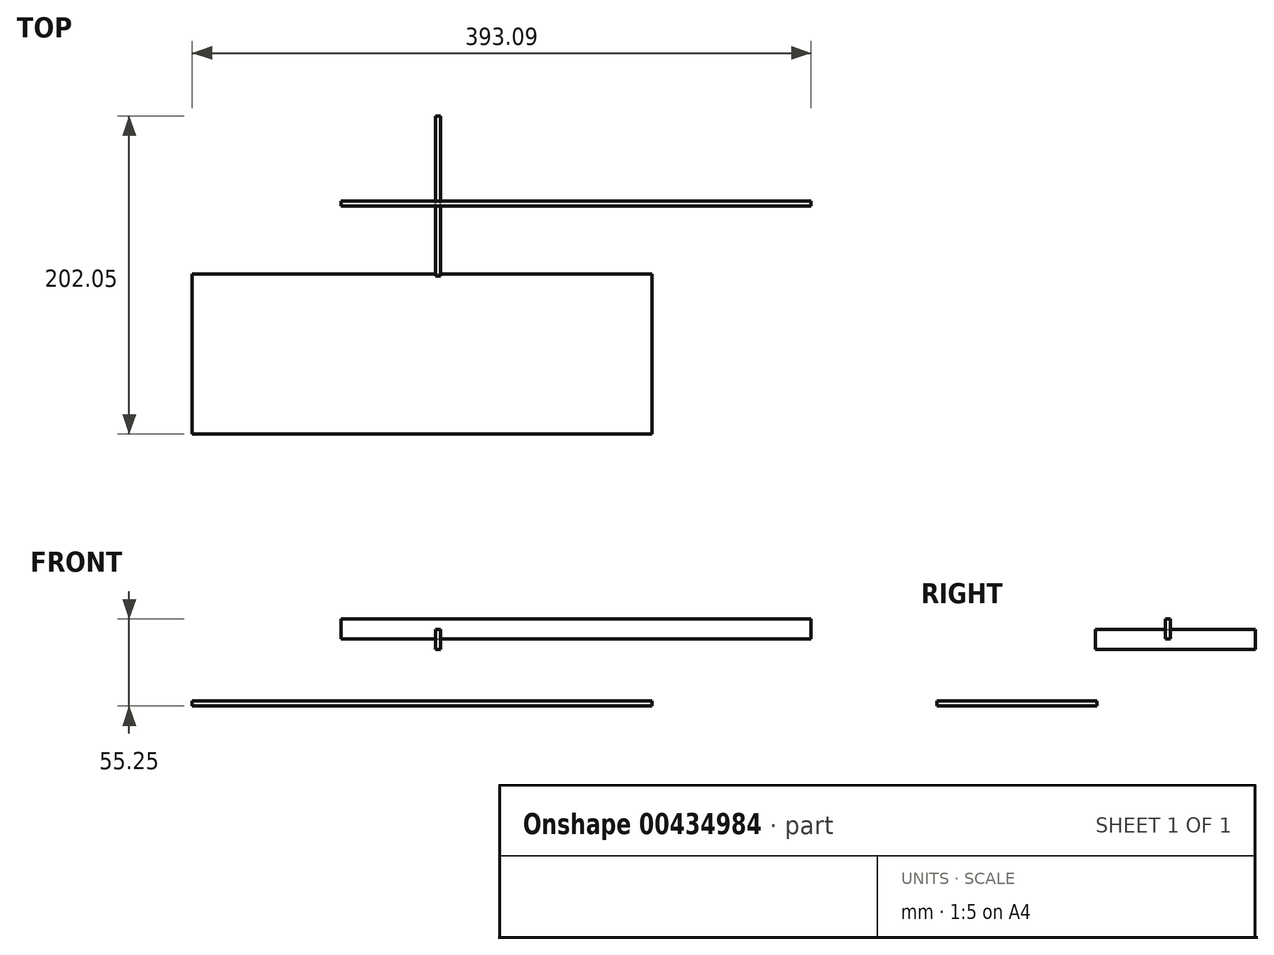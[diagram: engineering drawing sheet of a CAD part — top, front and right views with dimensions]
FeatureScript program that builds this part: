
annotation { "Feature Type Name" : "Feature", "Feature Type Description" : "" }
export const myFeature = defineFeature(function(context is Context, id is Id, definition is map)
    precondition{}
    {
        {
            var Q0;
            Q0=qCreatedBy(makeId("Top.planeOp"),FACE);
            var sketch = newSketch(context, id + "F0", { "sketchPlane" : qUnion([Q0])});
            skLineSegment(sketch, "E0.bottom", {"start": v(-154.5, -148.06) * mm, "end": v(137.6, -148.06) * mm});
            skLineSegment(sketch, "E0.top", {"start": v(-154.5, -46.46) * mm, "end": v(137.6, -46.46) * mm});
            skLineSegment(sketch, "E0.left", {"start": v(-154.5, -148.06) * mm, "end": v(-154.5, -46.46) * mm});
            skLineSegment(sketch, "E0.right", {"start": v(137.6, -148.06) * mm, "end": v(137.6, -46.46) * mm});
            skSolve(sketch);
        }
        {
            var Q0;
            Q0=makeQuery(id+"F0.imprint","IMPRINT",FACE,{"disambiguationData":[TD([[makeQuery(id+"F0.imprint","IMPRINT",EDGE,{"derivedFrom":sQuery(id+"F0.wireOp",EDGE,"E0.bottom")}),1.0]])]});
            extrude(context, id + "F1", {"entities" : qUnion([Q0]), "depth" : 3.17 * mm});
        }
        {
            var Q0;
            Q0=qCreatedBy(makeId("Front.planeOp"),FACE);
            var sketch = newSketch(context, id + "F2", { "sketchPlane" : qUnion([Q0])});
            skLineSegment(sketch, "E1.bottom", {"start": v(-59.85, 55.25) * mm, "end": v(238.6, 55.25) * mm});
            skLineSegment(sketch, "E1.top", {"start": v(-59.85, 42.55) * mm, "end": v(238.6, 42.55) * mm});
            skLineSegment(sketch, "E1.left", {"start": v(-59.85, 55.25) * mm, "end": v(-59.85, 42.55) * mm});
            skLineSegment(sketch, "E1.right", {"start": v(238.6, 55.25) * mm, "end": v(238.6, 42.55) * mm});
            skSolve(sketch);
        }
        {
            var Q0;
            Q0 = qSketchRegion(id + "F2", true);
            extrude(context, id + "F3", {"entities" : qUnion([Q0]), "depth" : 3.17 * mm});
        }
        {
            var Q0;
            Q0=qCreatedBy(makeId("Right.planeOp"),FACE);
            var sketch = newSketch(context, id + "F4", { "sketchPlane" : qUnion([Q0])});
            skLineSegment(sketch, "E2.bottom", {"start": v(-47.61, 48.7) * mm, "end": v(53.99, 48.7) * mm});
            skLineSegment(sketch, "E2.top", {"start": v(-47.61, 36) * mm, "end": v(53.99, 36) * mm});
            skLineSegment(sketch, "E2.left", {"start": v(-47.61, 48.7) * mm, "end": v(-47.61, 36) * mm});
            skLineSegment(sketch, "E2.right", {"start": v(53.99, 48.7) * mm, "end": v(53.99, 36) * mm});
            skSolve(sketch);
        }
        {
            var Q0;
            Q0 = qSketchRegion(id + "F4", true);
            extrude(context, id + "F5", {"entities" : qUnion([Q0]), "depth" : 3.17 * mm});
        }
    });
